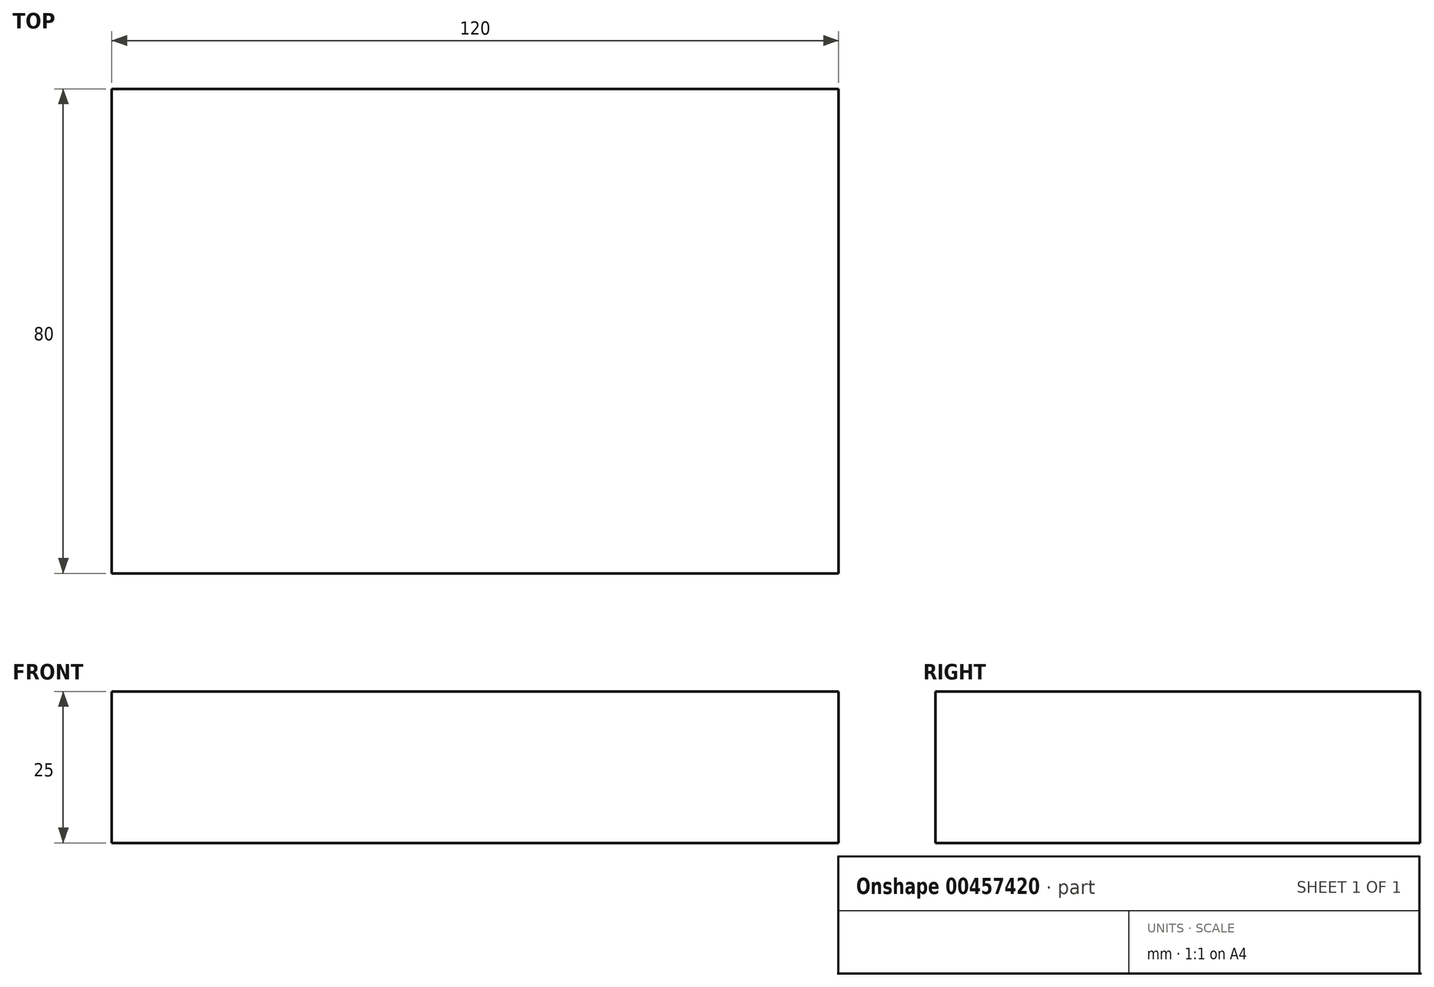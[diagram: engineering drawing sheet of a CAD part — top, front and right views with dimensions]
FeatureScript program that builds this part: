
annotation { "Feature Type Name" : "Feature", "Feature Type Description" : "" }
export const myFeature = defineFeature(function(context is Context, id is Id, definition is map)
    precondition{}
    {
        {
            var Q0;
            Q0=qCreatedBy(makeId("Top.planeOp"),FACE);
            var sketch = newSketch(context, id + "F0", { "sketchPlane" : qUnion([Q0])});
            skLineSegment(sketch, "E0.bottom", {"start": v(-30.69, 56.34) * mm, "end": v(89.31, 56.34) * mm});
            skLineSegment(sketch, "E0.top", {"start": v(-30.69, -23.66) * mm, "end": v(89.31, -23.66) * mm});
            skLineSegment(sketch, "E0.left", {"start": v(-30.69, 56.34) * mm, "end": v(-30.69, -23.66) * mm});
            skLineSegment(sketch, "E0.right", {"start": v(89.31, 56.34) * mm, "end": v(89.31, -23.66) * mm});
            skSolve(sketch);
        }
        {
            var Q0;
            Q0=makeQuery(id+"F0.imprint","IMPRINT",FACE,{"disambiguationData":[TD([[makeQuery(id+"F0.imprint","IMPRINT",EDGE,{"derivedFrom":sQuery(id+"F0.wireOp",EDGE,"E0.bottom")}),-1.0]])]});
            extrude(context, id + "F1", {"entities" : qUnion([Q0]), "depth" : 25 * mm});
        }
    });
